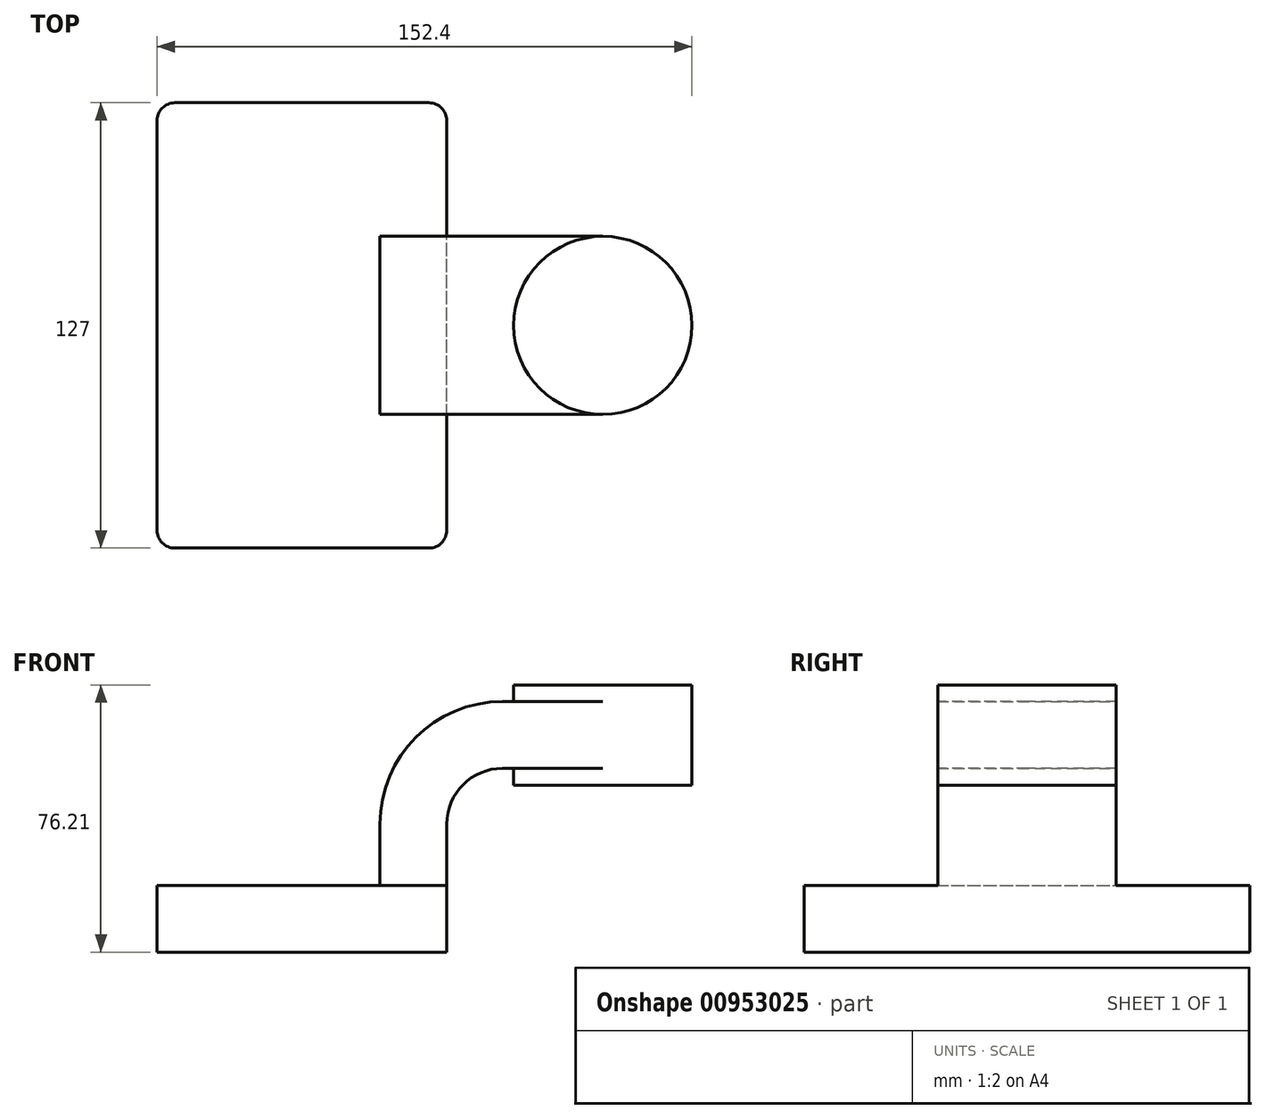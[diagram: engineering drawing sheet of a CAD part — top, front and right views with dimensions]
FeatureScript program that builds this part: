
annotation { "Feature Type Name" : "Feature", "Feature Type Description" : "" }
export const myFeature = defineFeature(function(context is Context, id is Id, definition is map)
    precondition{}
    {
        {
            var Q0;
            Q0=qCreatedBy(makeId("Front.planeOp"),FACE);
            var sketch = newSketch(context, id + "F0", { "sketchPlane" : qUnion([Q0])});
            skLineSegment(sketch, "E0.bottom", {"start": v(-41.28, 9.52) * mm, "end": v(41.27, 9.53) * mm});
            skLineSegment(sketch, "E0.top", {"start": v(-41.28, -9.53) * mm, "end": v(41.28, -9.53) * mm});
            skLineSegment(sketch, "E0.left", {"start": v(-41.28, 9.52) * mm, "end": v(-41.27, -9.53) * mm});
            skLineSegment(sketch, "E0.right", {"start": v(41.28, 9.53) * mm, "end": v(41.28, -9.52) * mm});
            skPoint(sketch, "E0.middle", {"position": v(0, 0) * mm});
            skLineSegment(sketch, "E1.bottom", {"start": v(60.32, 38.1) * mm, "end": v(111.12, 38.1) * mm});
            skLineSegment(sketch, "E1.top", {"start": v(60.33, 66.68) * mm, "end": v(111.12, 66.68) * mm});
            skLineSegment(sketch, "E1.left", {"start": v(60.32, 38.1) * mm, "end": v(60.32, 66.68) * mm});
            skLineSegment(sketch, "E1.right", {"start": v(111.12, 38.1) * mm, "end": v(111.12, 66.68) * mm});
            skPoint(sketch, "E1.middle", {"position": v(85.72, 52.39) * mm});
            skLineSegment(sketch, "E2", {"start": v(41.27, 9.53) * mm, "end": v(41.27, 27) * mm});
            skArc(sketch, "E3", {"start": v(41.27, 27) * mm, "mid": v(45.92, 38.23) * mm, "end": v(57.15, 42.88) * mm});
            skLineSegment(sketch, "E4", {"start": v(57.15, 42.88) * mm, "end": v(85.72, 42.88) * mm});
            skLineSegment(sketch, "E5.0", {"start": v(57.15, 61.93) * mm, "end": v(85.72, 61.93) * mm});
            skArc(sketch, "E5.1", {"start": v(22.23, 27) * mm, "mid": v(32.45, 51.7) * mm, "end": v(57.15, 61.93) * mm});
            skLineSegment(sketch, "E5.2", {"start": v(22.22, 9.53) * mm, "end": v(22.22, 27) * mm});
            skFitSpline(sketch, "E6", {"points": [v(-41.28, 9.53) * mm, v(57.15, 61.93) * mm], "startDerivative": vector(-1.27, 106.25) * mm, "endDerivative": vector(136.48, -0.76) * mm});
            skLineSegment(sketch, "E7", {"start": v(85.72, 38.1) * mm, "end": v(85.72, 66.68) * mm});
            skSolve(sketch);
        }
        {
            var Q0;
            Q0=makeQuery(id+"F0.imprint","IMPRINT",FACE,{"disambiguationData":[TD([[makeQuery(id+"F0.imprint","IMPRINT",EDGE,{"derivedFrom":sQuery(id+"F0.wireOp",EDGE,"E0.top")}),1.0]])]});
            extrude(context, id + "F1", {"entities" : qUnion([Q0]), "endBound" : BoundingType.SYMMETRIC, "depth" : 127 * mm, "offsetDistance" : 25.4 * mm});
        }
        {
            var Q0;
            {var subQ1=sQuery(id+"F0.wireOp",EDGE,"E2");Q0=makeQuery(id+"F0.imprint","IMPRINT",FACE,{"disambiguationData":[TD([[makeQuery(id+"F0.imprint","IMPRINT",EDGE,{"derivedFrom":subQ1}),1.0]])]});}
            var Q1;
            {var subQ0=sQuery(id+"F0.wireOp",EDGE,"E4");var subQ1=sQuery(id+"F0.wireOp",EDGE,"E1.left");var subQ2=makeQuery(id+"F0.imprint","INTERSECT",VERTEX,{"derivedFrom":[subQ1,subQ0]});Q1=makeQuery(id+"F0.imprint","IMPRINT",FACE,{"disambiguationData":[TD([[makeQuery(id+"F0.imprint","IMPRINT",EDGE,{"disambiguationData":[TD([[subQ2,-1.0]])],"derivedFrom":subQ1}),-1.0]])]});}
            extrude(context, id + "F2", {"entities" : qUnion([Q0, Q1]), "operationType" : NewBodyOperationType.ADD, "endBound" : BoundingType.SYMMETRIC, "depth" : 50.8 * mm, "offsetDistance" : 25.4 * mm});
        }
        {
            var Q0;
            Q0=makeQuery(id+"F0.imprint","IMPRINT",FACE,{"disambiguationData":[TD([[makeQuery(id+"F0.imprint","IMPRINT",EDGE,{"derivedFrom":sQuery(id+"F0.wireOp",EDGE,"E5.1")}),1.0]])]});
            extrude(context, id + "F3", {"entities" : qUnion([Q0]), "operationType" : NewBodyOperationType.ADD, "endBound" : BoundingType.SYMMETRIC, "depth" : 15.88 * mm, "offsetDistance" : 25.4 * mm});
        }
        {
            var Q0;
            {var subQ4=sQuery(id+"F0.wireOp",EDGE,"E1.right");Q0=makeQuery(id+"F0.imprint","IMPRINT",FACE,{"disambiguationData":[TD([[makeQuery(id+"F0.imprint","IMPRINT",EDGE,{"derivedFrom":subQ4}),1.0]])]});}
            var Q1;
            Q1=sQuery(id+"F0.wireOp",EDGE,"E7");
            revolve(context, id + "F4", {"operationType" : NewBodyOperationType.ADD, "surfaceOperationType" : NewSurfaceOperationType.NEW, "entities" : qUnion([Q0]), "axis" : qUnion([Q1]), "revolveType" : RevolveType.FULL});
        }
        {
            var Q0;
            Q0=makeQuery(id+"F1.opExtrude","CAP_EDGE",EDGE,{"disambiguationData":[OSD([sQuery(id+"F0.wireOp",EDGE,"E0.left")])],"isStart":true});
            var Q1;
            Q1=makeQuery(id+"F1.opExtrude","CAP_EDGE",EDGE,{"disambiguationData":[OSD([sQuery(id+"F0.wireOp",EDGE,"E0.left")])],"isStart":false});
            var Q2;
            Q2=makeQuery(id+"F1.opExtrude","CAP_EDGE",EDGE,{"disambiguationData":[OSD([sQuery(id+"F0.wireOp",EDGE,"E0.right")])],"isStart":false});
            var Q3;
            Q3=makeQuery(id+"F1.opExtrude","CAP_EDGE",EDGE,{"disambiguationData":[OSD([sQuery(id+"F0.wireOp",EDGE,"E0.right")])],"isStart":true});
            fillet(context, id + "F5", {"entities" : qUnion([Q0, Q1, Q2, Q3]), "radius" : 5.08 * mm, "tangentPropagation" : true, "allowEdgeOverflow" : false});
        }
    });
